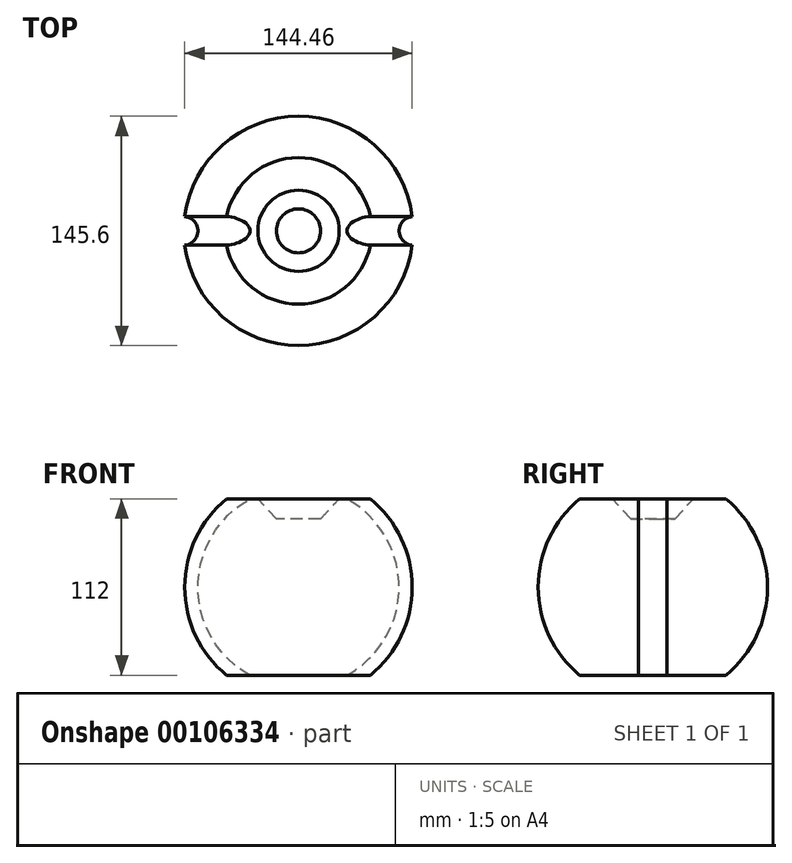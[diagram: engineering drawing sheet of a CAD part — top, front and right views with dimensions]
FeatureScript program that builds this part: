
annotation { "Feature Type Name" : "Feature", "Feature Type Description" : "" }
export const myFeature = defineFeature(function(context is Context, id is Id, definition is map)
    precondition{}
    {
        {
            var Q0;
            Q0=qCreatedBy(makeId("Front.planeOp"),FACE);
            var sketch = newSketch(context, id + "F0", { "sketchPlane" : qUnion([Q0])});
            skArc(sketch, "E0", {"start": v(-46.53, 56) * mm, "mid": v(-72.8, 0) * mm, "end": v(-46.53, -56) * mm});
            skLineSegment(sketch, "E1", {"start": v(0, 72.8) * mm, "end": v(0, -77.48) * mm});
            skLineSegment(sketch, "E2", {"start": v(-46.53, 56) * mm, "end": v(0, 56) * mm});
            skLineSegment(sketch, "E3.MirrorCS", {"start": v(-46.53, -56) * mm, "end": v(0, -56) * mm});
            skPoint(sketch, "E4.orphan", {"position": v(46.53, -56) * mm});
            skPoint(sketch, "E5.orphan", {"position": v(46.53, 56) * mm});
            skSolve(sketch);
        }
        {
            var Q0;
            Q0=makeQuery(id+"F0.imprint","IMPRINT",FACE,{"disambiguationData":[TD([[makeQuery(id+"F0.imprint","IMPRINT",EDGE,{"derivedFrom":sQuery(id+"F0.wireOp",EDGE,"E0")}),1.0]])]});
            var Q1;
            Q1=sQuery(id+"F0.wireOp",EDGE,"E1");
            revolve(context, id + "F1", {"entities" : qUnion([Q0]), "axis" : qUnion([Q1]), "revolveType" : RevolveType.FULL});
        }
        {
            var Q0;
            Q0=qCreatedBy(makeId("Top.planeOp"),FACE);
            var sketch = newSketch(context, id + "F2", { "sketchPlane" : qUnion([Q0])});
            skCircle(sketch, "E6", {"center": v(-72.95, 0) * mm, "radius": 9.1 * mm});
            skLineSegment(sketch, "E7", {"start": v(0, 0) * mm, "end": v(0, 90.3) * mm, "construction": true});
            skLineSegment(sketch, "E8", {"start": v(0, 0) * mm, "end": v(0, -107.65) * mm, "construction": true});
            skSolve(sketch);
        }
        {
            var Q0;
            Q0 = qSketchRegion(id + "F2", true);
            var Q1;
            Q1=sQuery(id+"F2.wireOp",EDGE,"E8");
            revolve(context, id + "F3", {"operationType" : NewBodyOperationType.REMOVE, "entities" : qUnion([Q0]), "axis" : qUnion([Q1]), "revolveType" : RevolveType.FULL, "oppositeDirection" : true});
        }
        {
            var Q0;
            Q0=makeQuery(id+"F1.opRevolve","SWEPT_FACE",FACE,{"disambiguationData":[OSD([sQuery(id+"F0.wireOp",EDGE,"E2")])]});
            cPlane(context, id + "F4", {"entities" : qUnion([Q0]), "cplaneType" : CPlaneType.OFFSET, "offset" : 12.7 * mm, "oppositeDirection" : true, "width" : 152.4 * mm, "height" : 152.4 * mm});
        }
        {
            var Q0;
            Q0=makeQuery(id+"F1.opRevolve","SWEPT_FACE",FACE,{"disambiguationData":[OSD([sQuery(id+"F0.wireOp",EDGE,"E2")])]});
            var sketch = newSketch(context, id + "F5", { "sketchPlane" : qUnion([Q0])});
            skCircle(sketch, "E9", {"center": v(0, 0) * mm, "radius": 25.78 * mm});
            skSolve(sketch);
        }
        {
            var Q0;
            Q0=qCreatedBy(id+"F4.planeOp",FACE);
            var sketch = newSketch(context, id + "F6", { "sketchPlane" : qUnion([Q0])});
            skCircle(sketch, "E10", {"center": v(0, 0) * mm, "radius": 13.98 * mm});
            skSolve(sketch);
        }
        {
            var Q1;
            Q1=makeQuery(id+"F5.imprint","IMPRINT",FACE,{"disambiguationData":[TD([[makeQuery(id+"F5.imprint","IMPRINT",EDGE,{"derivedFrom":sQuery(id+"F5.wireOp",EDGE,"E9")}),1.0]])]});
            var Q2;
            Q2 = qSketchRegion(id + "F6", true);
            loft(context, id + "F7", {"operationType" : NewBodyOperationType.REMOVE, "sheetProfilesArray" : [{ "sheetProfileEntities" : qUnion([Q1]) }, { "sheetProfileEntities" : qUnion([Q2]) }]});
        }
    });
